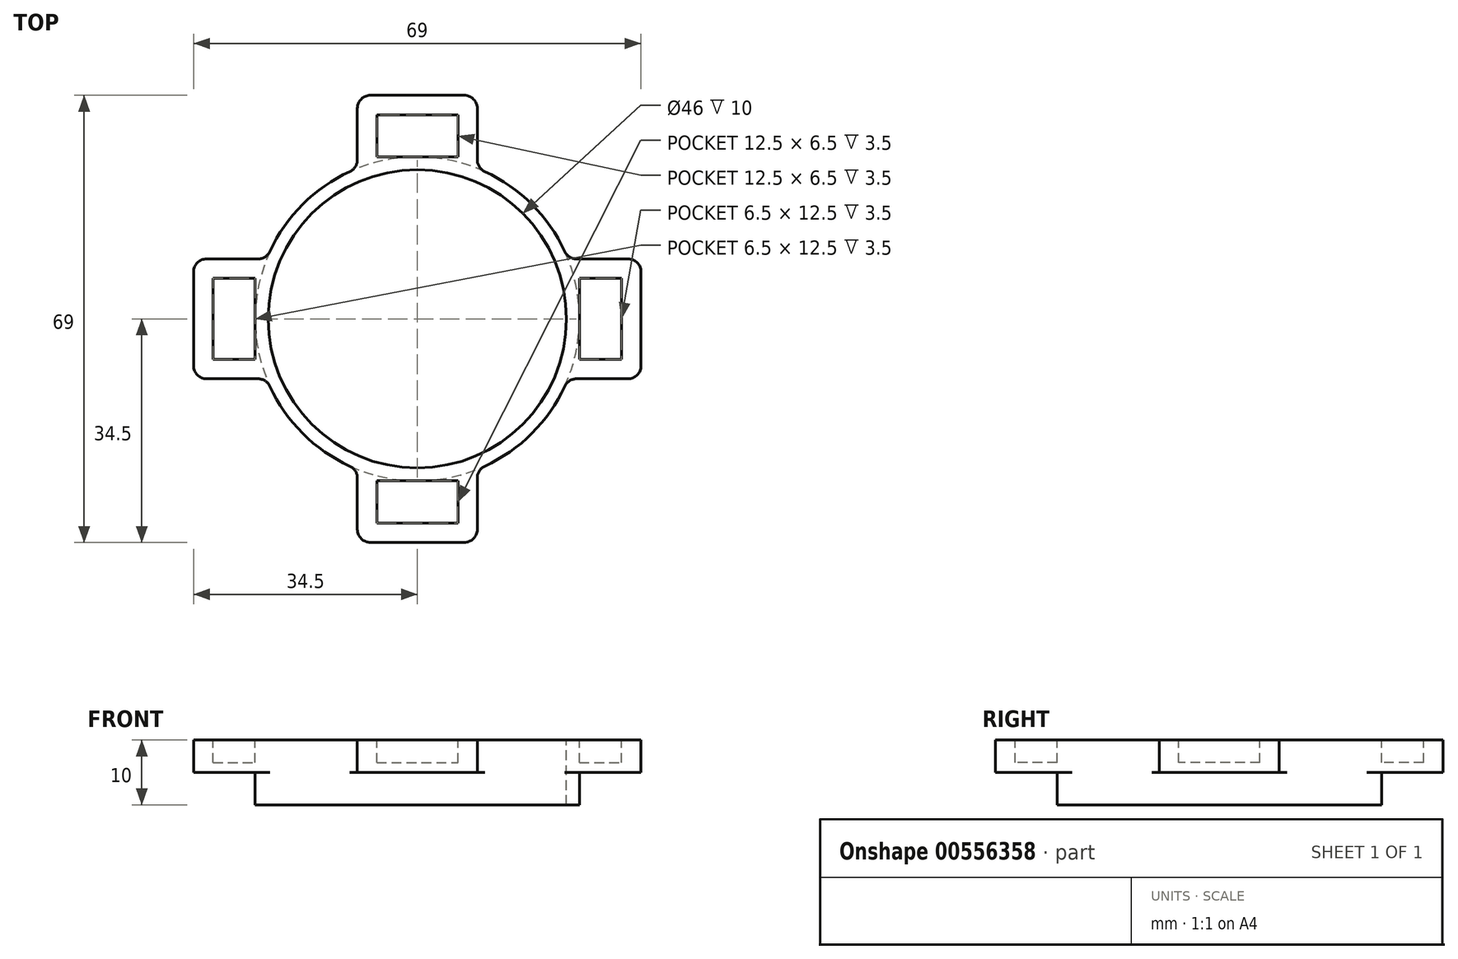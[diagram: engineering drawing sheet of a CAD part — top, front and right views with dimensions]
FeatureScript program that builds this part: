
annotation { "Feature Type Name" : "Feature", "Feature Type Description" : "" }
export const myFeature = defineFeature(function(context is Context, id is Id, definition is map)
    precondition{}
    {
        {
            var Q0;
            Q0=qCreatedBy(makeId("Top.planeOp"),FACE);
            var sketch = newSketch(context, id + "F0", { "sketchPlane" : qUnion([Q0])});
            skCircle(sketch, "E0", {"center": v(0, 0) * mm, "radius": 31.75 * mm, "construction": true});
            skCircle(sketch, "E1", {"center": v(0, 0) * mm, "radius": 23 * mm});
            skLineSegment(sketch, "E2.bottom", {"start": v(25, 6.25) * mm, "end": v(31.5, 6.25) * mm});
            skLineSegment(sketch, "E2.top", {"start": v(25, -6.25) * mm, "end": v(31.5, -6.25) * mm});
            skLineSegment(sketch, "E2.left", {"start": v(25, 6.25) * mm, "end": v(25, -6.25) * mm});
            skLineSegment(sketch, "E2.right", {"start": v(31.5, 6.25) * mm, "end": v(31.5, -6.25) * mm});
            skPoint(sketch, "E3", {"position": v(25, 0) * mm});
            skCircle(sketch, "E4", {"center": v(0, 0) * mm, "radius": 25 * mm});
            skLineSegment(sketch, "E5.bottom", {"start": v(-31.5, 6.25) * mm, "end": v(-25, 6.25) * mm});
            skLineSegment(sketch, "E5.top", {"start": v(-31.5, -6.25) * mm, "end": v(-25, -6.25) * mm});
            skLineSegment(sketch, "E5.left", {"start": v(-31.5, 6.25) * mm, "end": v(-31.5, -6.25) * mm});
            skLineSegment(sketch, "E5.right", {"start": v(-25, 6.25) * mm, "end": v(-25, -6.25) * mm});
            skPoint(sketch, "E6", {"position": v(-25, 0) * mm});
            skLineSegment(sketch, "E7.bottom", {"start": v(-34.5, 9.25) * mm, "end": v(34.5, 9.25) * mm});
            skLineSegment(sketch, "E7.top", {"start": v(-34.5, -9.25) * mm, "end": v(34.5, -9.25) * mm});
            skLineSegment(sketch, "E7.left", {"start": v(-34.5, 9.25) * mm, "end": v(-34.5, -9.25) * mm});
            skLineSegment(sketch, "E7.right", {"start": v(34.5, 9.25) * mm, "end": v(34.5, -9.25) * mm});
            skCircle(sketch, "E8", {"center": v(0, 0) * mm, "radius": 19.05 * mm});
            skLineSegment(sketch, "E9.bottom", {"start": v(-9.25, 34.5) * mm, "end": v(9.25, 34.5) * mm});
            skLineSegment(sketch, "E9.top", {"start": v(-9.25, -34.5) * mm, "end": v(9.25, -34.5) * mm});
            skLineSegment(sketch, "E9.left", {"start": v(-9.25, 34.5) * mm, "end": v(-9.25, -34.5) * mm});
            skLineSegment(sketch, "E9.right", {"start": v(9.25, 34.5) * mm, "end": v(9.25, -34.5) * mm});
            skLineSegment(sketch, "E10.bottom", {"start": v(-6.25, 31.5) * mm, "end": v(6.25, 31.5) * mm});
            skLineSegment(sketch, "E10.top", {"start": v(-6.25, 25) * mm, "end": v(6.25, 25) * mm});
            skLineSegment(sketch, "E10.left", {"start": v(-6.25, 31.5) * mm, "end": v(-6.25, 25) * mm});
            skLineSegment(sketch, "E10.right", {"start": v(6.25, 31.5) * mm, "end": v(6.25, 25) * mm});
            skLineSegment(sketch, "E11.bottom", {"start": v(-6.25, -25) * mm, "end": v(6.25, -25) * mm});
            skLineSegment(sketch, "E11.top", {"start": v(-6.25, -31.5) * mm, "end": v(6.25, -31.5) * mm});
            skLineSegment(sketch, "E11.left", {"start": v(-6.25, -25) * mm, "end": v(-6.25, -31.5) * mm});
            skLineSegment(sketch, "E11.right", {"start": v(6.25, -25) * mm, "end": v(6.25, -31.5) * mm});
            skPoint(sketch, "E12", {"position": v(0, -25) * mm});
            skSolve(sketch);
        }
        {
            var Q0;
            {var subQ0=sQuery(id+"F0.wireOp",EDGE,"E5.bottom");Q0=makeQuery(id+"F0.imprint","IMPRINT",FACE,{"disambiguationData":[TD([[makeQuery(id+"F0.imprint","IMPRINT",EDGE,{"derivedFrom":subQ0}),1.0]])]});}
            var Q1;
            {var subQ4=sQuery(id+"F0.wireOp",EDGE,"E2.bottom");Q1=makeQuery(id+"F0.imprint","IMPRINT",FACE,{"disambiguationData":[TD([[makeQuery(id+"F0.imprint","IMPRINT",EDGE,{"derivedFrom":subQ4}),1.0]])]});}
            var Q2;
            {var subQ0=sQuery(id+"F0.wireOp",EDGE,"E7.top");var subQ1=sQuery(id+"F0.wireOp",EDGE,"9AU1a6xc-WkkM-5iDV-fBZs-smRrCXbzpLaA");var subQ2=makeQuery(id+"F0.imprint","INTERSECT",VERTEX,{"disambiguationData":[OD(0.0)],"derivedFrom":[subQ1,subQ0]});Q2=makeQuery(id+"F0.imprint","IMPRINT",FACE,{"disambiguationData":[TD([[makeQuery(id+"F0.imprint","IMPRINT",EDGE,{"disambiguationData":[TD([[subQ2,-1.0]])],"derivedFrom":subQ1}),-1.0]])]});}
            var Q3;
            {var subQ0=sQuery(id+"F0.wireOp",EDGE,"E7.bottom");var subQ3=sQuery(id+"F0.wireOp",EDGE,"9AU1a6xc-WkkM-5iDV-fBZs-smRrCXbzpLaA");var subQ4=makeQuery(id+"F0.imprint","INTERSECT",VERTEX,{"disambiguationData":[OD(1.0)],"derivedFrom":[subQ3,subQ0]});Q3=makeQuery(id+"F0.imprint","IMPRINT",FACE,{"disambiguationData":[TD([[makeQuery(id+"F0.imprint","IMPRINT",EDGE,{"disambiguationData":[TD([[subQ4,1.0]])],"derivedFrom":subQ3}),-1.0]])]});}
            var Q4;
            {var subQ0=sQuery(id+"F0.wireOp",EDGE,"E7.bottom");var subQ1=sQuery(id+"F0.wireOp",EDGE,"9AU1a6xc-WkkM-5iDV-fBZs-smRrCXbzpLaA");var subQ2=makeQuery(id+"F0.imprint","INTERSECT",VERTEX,{"disambiguationData":[OD(0.0)],"derivedFrom":[subQ1,subQ0]});Q4=makeQuery(id+"F0.imprint","IMPRINT",FACE,{"disambiguationData":[TD([[makeQuery(id+"F0.imprint","IMPRINT",EDGE,{"disambiguationData":[TD([[subQ2,1.0]])],"derivedFrom":subQ1}),-1.0]])]});}
            var Q5;
            {var subQ0=sQuery(id+"F0.wireOp",EDGE,"E7.bottom");var subQ3=sQuery(id+"F0.wireOp",EDGE,"9AU1a6xc-WkkM-5iDV-fBZs-smRrCXbzpLaA");var subQ4=makeQuery(id+"F0.imprint","INTERSECT",VERTEX,{"disambiguationData":[OD(0.0)],"derivedFrom":[subQ3,subQ0]});Q5=makeQuery(id+"F0.imprint","IMPRINT",FACE,{"disambiguationData":[TD([[makeQuery(id+"F0.imprint","IMPRINT",EDGE,{"disambiguationData":[TD([[subQ4,-1.0]])],"derivedFrom":subQ3}),-1.0]])]});}
            var Q6;
            {var subQ0=sQuery(id+"F0.wireOp",EDGE,"E7.bottom");var subQ1=sQuery(id+"F0.wireOp",EDGE,"9AU1a6xc-WkkM-5iDV-fBZs-smRrCXbzpLaA");var subQ2=makeQuery(id+"F0.imprint","INTERSECT",VERTEX,{"disambiguationData":[OD(0.0)],"derivedFrom":[subQ1,subQ0]});Q6=makeQuery(id+"F0.imprint","IMPRINT",FACE,{"disambiguationData":[TD([[makeQuery(id+"F0.imprint","IMPRINT",EDGE,{"disambiguationData":[TD([[subQ2,-1.0]])],"derivedFrom":subQ1}),1.0]])]});}
            var Q7;
            {var subQ0=sQuery(id+"F0.wireOp",EDGE,"E7.bottom");var subQ1=sQuery(id+"F0.wireOp",EDGE,"9AU1a6xc-WkkM-5iDV-fBZs-smRrCXbzpLaA");var subQ2=makeQuery(id+"F0.imprint","INTERSECT",VERTEX,{"disambiguationData":[OD(1.0)],"derivedFrom":[subQ1,subQ0]});Q7=makeQuery(id+"F0.imprint","IMPRINT",FACE,{"disambiguationData":[TD([[makeQuery(id+"F0.imprint","IMPRINT",EDGE,{"disambiguationData":[TD([[subQ2,1.0]])],"derivedFrom":subQ1}),1.0]])]});}
            var Q8;
            {var subQ0=sQuery(id+"F0.wireOp",EDGE,"E7.bottom");var subQ1=sQuery(id+"F0.wireOp",EDGE,"9AU1a6xc-WkkM-5iDV-fBZs-smRrCXbzpLaA");var subQ2=makeQuery(id+"F0.imprint","INTERSECT",VERTEX,{"disambiguationData":[OD(0.0)],"derivedFrom":[subQ1,subQ0]});Q8=makeQuery(id+"F0.imprint","IMPRINT",FACE,{"disambiguationData":[TD([[makeQuery(id+"F0.imprint","IMPRINT",EDGE,{"disambiguationData":[TD([[subQ2,1.0]])],"derivedFrom":subQ1}),1.0]])]});}
            var Q9;
            {var subQ0=sQuery(id+"F0.wireOp",EDGE,"E7.top");var subQ1=sQuery(id+"F0.wireOp",EDGE,"9AU1a6xc-WkkM-5iDV-fBZs-smRrCXbzpLaA");var subQ2=makeQuery(id+"F0.imprint","INTERSECT",VERTEX,{"disambiguationData":[OD(0.0)],"derivedFrom":[subQ1,subQ0]});Q9=makeQuery(id+"F0.imprint","IMPRINT",FACE,{"disambiguationData":[TD([[makeQuery(id+"F0.imprint","IMPRINT",EDGE,{"disambiguationData":[TD([[subQ2,-1.0]])],"derivedFrom":subQ1}),1.0]])]});}
            var Q10;
            {var subQ1=sQuery(id+"F0.wireOp",EDGE,"E5.bottom");Q10=makeQuery(id+"F0.imprint","IMPRINT",FACE,{"disambiguationData":[TD([[makeQuery(id+"F0.imprint","IMPRINT",EDGE,{"derivedFrom":subQ1}),-1.0]])]});}
            var Q11;
            {var subQ3=sQuery(id+"F0.wireOp",EDGE,"E2.bottom");Q11=makeQuery(id+"F0.imprint","IMPRINT",FACE,{"disambiguationData":[TD([[makeQuery(id+"F0.imprint","IMPRINT",EDGE,{"derivedFrom":subQ3}),-1.0]])]});}
            var Q12;
            {var subQ0=sQuery(id+"F0.wireOp",EDGE,"E7.bottom");var subQ1=sQuery(id+"F0.wireOp",EDGE,"E1");var subQ2=makeQuery(id+"F0.imprint","INTERSECT",VERTEX,{"disambiguationData":[OD(0.0)],"derivedFrom":[subQ1,subQ0]});Q12=makeQuery(id+"F0.imprint","IMPRINT",FACE,{"disambiguationData":[TD([[makeQuery(id+"F0.imprint","IMPRINT",EDGE,{"disambiguationData":[TD([[subQ2,1.0]])],"derivedFrom":subQ1}),-1.0]])]});}
            var Q13;
            {var subQ4=sQuery(id+"F0.wireOp",EDGE,"E7.bottom");var subQ5=sQuery(id+"F0.wireOp",EDGE,"E1");var subQ6=makeQuery(id+"F0.imprint","INTERSECT",VERTEX,{"disambiguationData":[OD(0.0)],"derivedFrom":[subQ5,subQ4]});Q13=makeQuery(id+"F0.imprint","IMPRINT",FACE,{"disambiguationData":[TD([[makeQuery(id+"F0.imprint","IMPRINT",EDGE,{"disambiguationData":[TD([[subQ6,-1.0]])],"derivedFrom":subQ5}),-1.0]])]});}
            var Q14;
            {var subQ4=sQuery(id+"F0.wireOp",EDGE,"E7.bottom");var subQ5=sQuery(id+"F0.wireOp",EDGE,"E1");var subQ6=makeQuery(id+"F0.imprint","INTERSECT",VERTEX,{"disambiguationData":[OD(1.0)],"derivedFrom":[subQ5,subQ4]});Q14=makeQuery(id+"F0.imprint","IMPRINT",FACE,{"disambiguationData":[TD([[makeQuery(id+"F0.imprint","IMPRINT",EDGE,{"disambiguationData":[TD([[subQ6,1.0]])],"derivedFrom":subQ5}),-1.0]])]});}
            var Q15;
            {var subQ0=sQuery(id+"F0.wireOp",EDGE,"E7.top");var subQ1=sQuery(id+"F0.wireOp",EDGE,"E1");var subQ2=makeQuery(id+"F0.imprint","INTERSECT",VERTEX,{"disambiguationData":[OD(0.0)],"derivedFrom":[subQ1,subQ0]});Q15=makeQuery(id+"F0.imprint","IMPRINT",FACE,{"disambiguationData":[TD([[makeQuery(id+"F0.imprint","IMPRINT",EDGE,{"disambiguationData":[TD([[subQ2,-1.0]])],"derivedFrom":subQ1}),-1.0]])]});}
            var Q16;
            {var subQ0=sQuery(id+"F0.wireOp",EDGE,"E7.bottom");var subQ3=sQuery(id+"F0.wireOp",EDGE,"E1");var subQ4=makeQuery(id+"F0.imprint","INTERSECT",VERTEX,{"disambiguationData":[OD(1.0)],"derivedFrom":[subQ3,subQ0]});Q16=makeQuery(id+"F0.imprint","IMPRINT",FACE,{"disambiguationData":[TD([[makeQuery(id+"F0.imprint","IMPRINT",EDGE,{"disambiguationData":[TD([[subQ4,-1.0]])],"derivedFrom":subQ3}),-1.0]])]});}
            var Q17;
            {var subQ0=sQuery(id+"F0.wireOp",EDGE,"E9.right");var subQ4=sQuery(id+"F0.wireOp",EDGE,"E1");var subQ5=makeQuery(id+"F0.imprint","INTERSECT",VERTEX,{"disambiguationData":[OD(0.0)],"derivedFrom":[subQ4,subQ0]});Q17=makeQuery(id+"F0.imprint","IMPRINT",FACE,{"disambiguationData":[TD([[makeQuery(id+"F0.imprint","IMPRINT",EDGE,{"disambiguationData":[TD([[subQ5,-1.0]])],"derivedFrom":subQ4}),-1.0]])]});}
            var Q18;
            {var subQ0=sQuery(id+"F0.wireOp",EDGE,"E9.right");var subQ1=sQuery(id+"F0.wireOp",EDGE,"E1");var subQ2=makeQuery(id+"F0.imprint","INTERSECT",VERTEX,{"disambiguationData":[OD(1.0)],"derivedFrom":[subQ1,subQ0]});Q18=makeQuery(id+"F0.imprint","IMPRINT",FACE,{"disambiguationData":[TD([[makeQuery(id+"F0.imprint","IMPRINT",EDGE,{"disambiguationData":[TD([[subQ2,-1.0]])],"derivedFrom":subQ1}),-1.0]])]});}
            var Q19;
            {var subQ0=sQuery(id+"F0.wireOp",EDGE,"E9.left");var subQ3=sQuery(id+"F0.wireOp",EDGE,"E1");var subQ4=makeQuery(id+"F0.imprint","INTERSECT",VERTEX,{"disambiguationData":[OD(1.0)],"derivedFrom":[subQ3,subQ0]});Q19=makeQuery(id+"F0.imprint","IMPRINT",FACE,{"disambiguationData":[TD([[makeQuery(id+"F0.imprint","IMPRINT",EDGE,{"disambiguationData":[TD([[subQ4,-1.0]])],"derivedFrom":subQ3}),-1.0]])]});}
            var Q20;
            {var subQ1=sQuery(id+"F0.wireOp",EDGE,"E9.top");Q20=makeQuery(id+"F0.imprint","IMPRINT",FACE,{"disambiguationData":[TD([[makeQuery(id+"F0.imprint","IMPRINT",EDGE,{"derivedFrom":subQ1}),1.0]])]});}
            var Q21;
            Q21=makeQuery(id+"F0.imprint","IMPRINT",FACE,{"disambiguationData":[TD([[makeQuery(id+"F0.imprint","IMPRINT",EDGE,{"derivedFrom":sQuery(id+"F0.wireOp",EDGE,"E11.top")}),1.0]])]});
            var Q22;
            {var subQ0=sQuery(id+"F0.wireOp",EDGE,"E9.bottom");Q22=makeQuery(id+"F0.imprint","IMPRINT",FACE,{"disambiguationData":[TD([[makeQuery(id+"F0.imprint","IMPRINT",EDGE,{"derivedFrom":subQ0}),-1.0]])]});}
            var Q23;
            Q23=makeQuery(id+"F0.imprint","IMPRINT",FACE,{"disambiguationData":[TD([[makeQuery(id+"F0.imprint","IMPRINT",EDGE,{"derivedFrom":sQuery(id+"F0.wireOp",EDGE,"E10.bottom")}),-1.0]])]});
            extrude(context, id + "F1", {"entities" : qUnion([Q0, Q1, Q2, Q3, Q4, Q5, Q6, Q7, Q8, Q9, Q10, Q11, Q12, Q13, Q14, Q15, Q16, Q17, Q18, Q19, Q20, Q21, Q22, Q23]), "oppositeDirection" : true, "depth" : 5 * mm, "offsetDistance" : 25 * mm});
        }
        {
            var Q0;
            {var subQ1=sQuery(id+"F0.wireOp",EDGE,"E5.bottom");Q0=makeQuery(id+"F0.imprint","IMPRINT",FACE,{"disambiguationData":[TD([[makeQuery(id+"F0.imprint","IMPRINT",EDGE,{"derivedFrom":subQ1}),-1.0]])]});}
            var Q1;
            {var subQ3=sQuery(id+"F0.wireOp",EDGE,"E2.bottom");Q1=makeQuery(id+"F0.imprint","IMPRINT",FACE,{"disambiguationData":[TD([[makeQuery(id+"F0.imprint","IMPRINT",EDGE,{"derivedFrom":subQ3}),-1.0]])]});}
            var Q2;
            Q2=makeQuery(id+"F0.imprint","IMPRINT",FACE,{"disambiguationData":[TD([[makeQuery(id+"F0.imprint","IMPRINT",EDGE,{"derivedFrom":sQuery(id+"F0.wireOp",EDGE,"E10.bottom")}),-1.0]])]});
            var Q3;
            Q3=makeQuery(id+"F0.imprint","IMPRINT",FACE,{"disambiguationData":[TD([[makeQuery(id+"F0.imprint","IMPRINT",EDGE,{"derivedFrom":sQuery(id+"F0.wireOp",EDGE,"E11.top")}),1.0]])]});
            extrude(context, id + "F2", {"entities" : qUnion([Q0, Q1, Q2, Q3]), "operationType" : NewBodyOperationType.REMOVE, "oppositeDirection" : true, "depth" : 3.5 * mm, "offsetDistance" : 25 * mm});
        }
        {
            var Q0;
            Q0=makeQuery(id+"F1.opExtrude","SWEPT_EDGE",EDGE,{"disambiguationData":[OSD([sQuery(id+"F0.wireOp",EDGE,"E7.bottom"),sQuery(id+"F0.wireOp",EDGE,"E7.left")])]});
            var Q1;
            Q1=makeQuery(id+"F1.opExtrude","SWEPT_EDGE",EDGE,{"disambiguationData":[OSD([sQuery(id+"F0.wireOp",EDGE,"E7.top"),sQuery(id+"F0.wireOp",EDGE,"E7.left")])]});
            var Q2;
            Q2=makeQuery(id+"F1.opExtrude","SWEPT_EDGE",EDGE,{"disambiguationData":[OSD([sQuery(id+"F0.wireOp",EDGE,"E7.bottom"),sQuery(id+"F0.wireOp",EDGE,"E7.right")])]});
            var Q3;
            {var subQ0=sQuery(id+"F0.wireOp",EDGE,"E7.top");var subQ1=sQuery(id+"F0.wireOp",EDGE,"E4");Q3=makeQuery(id+"F1.opExtrude","SWEPT_EDGE",EDGE,{"disambiguationData":[OSD([subQ1,subQ0]),TDD([makeQuery(id+"F0.imprint","INTERSECT",VERTEX,{"disambiguationData":[OD(1.0)],"derivedFrom":[subQ1,subQ0]})])]});}
            var Q4;
            Q4=makeQuery(id+"F1.opExtrude","SWEPT_EDGE",EDGE,{"disambiguationData":[OSD([sQuery(id+"F0.wireOp",EDGE,"E7.top"),sQuery(id+"F0.wireOp",EDGE,"E7.right")])]});
            var Q5;
            {var subQ0=sQuery(id+"F0.wireOp",EDGE,"E7.top");var subQ1=sQuery(id+"F0.wireOp",EDGE,"E4");Q5=makeQuery(id+"F1.opExtrude","SWEPT_EDGE",EDGE,{"disambiguationData":[OSD([subQ1,subQ0]),TDD([makeQuery(id+"F0.imprint","INTERSECT",VERTEX,{"disambiguationData":[OD(0.0)],"derivedFrom":[subQ1,subQ0]})])]});}
            var Q6;
            {var subQ0=sQuery(id+"F0.wireOp",EDGE,"E7.bottom");var subQ1=sQuery(id+"F0.wireOp",EDGE,"E4");Q6=makeQuery(id+"F1.opExtrude","SWEPT_EDGE",EDGE,{"disambiguationData":[OSD([subQ1,subQ0]),TDD([makeQuery(id+"F0.imprint","INTERSECT",VERTEX,{"disambiguationData":[OD(0.0)],"derivedFrom":[subQ1,subQ0]})])]});}
            var Q7;
            Q7=makeQuery(id+"F1.opExtrude","SWEPT_EDGE",EDGE,{"disambiguationData":[OSD([sQuery(id+"F0.wireOp",EDGE,"E9.bottom"),sQuery(id+"F0.wireOp",EDGE,"E9.right")])]});
            var Q8;
            {var subQ0=sQuery(id+"F0.wireOp",EDGE,"E9.right");var subQ1=sQuery(id+"F0.wireOp",EDGE,"E4");Q8=makeQuery(id+"F1.opExtrude","SWEPT_EDGE",EDGE,{"disambiguationData":[OSD([subQ1,subQ0]),TDD([makeQuery(id+"F0.imprint","INTERSECT",VERTEX,{"disambiguationData":[OD(0.0)],"derivedFrom":[subQ1,subQ0]})])]});}
            var Q9;
            Q9=makeQuery(id+"F1.opExtrude","SWEPT_EDGE",EDGE,{"disambiguationData":[OSD([sQuery(id+"F0.wireOp",EDGE,"E9.top"),sQuery(id+"F0.wireOp",EDGE,"E9.right")])]});
            var Q10;
            Q10=makeQuery(id+"F1.opExtrude","SWEPT_EDGE",EDGE,{"disambiguationData":[OSD([sQuery(id+"F0.wireOp",EDGE,"E9.top"),sQuery(id+"F0.wireOp",EDGE,"E9.left")])]});
            var Q11;
            {var subQ0=sQuery(id+"F0.wireOp",EDGE,"E9.left");var subQ1=sQuery(id+"F0.wireOp",EDGE,"E4");Q11=makeQuery(id+"F1.opExtrude","SWEPT_EDGE",EDGE,{"disambiguationData":[OSD([subQ1,subQ0]),TDD([makeQuery(id+"F0.imprint","INTERSECT",VERTEX,{"disambiguationData":[OD(1.0)],"derivedFrom":[subQ1,subQ0]})])]});}
            var Q12;
            {var subQ0=sQuery(id+"F0.wireOp",EDGE,"E9.right");var subQ1=sQuery(id+"F0.wireOp",EDGE,"E4");Q12=makeQuery(id+"F1.opExtrude","SWEPT_EDGE",EDGE,{"disambiguationData":[OSD([subQ1,subQ0]),TDD([makeQuery(id+"F0.imprint","INTERSECT",VERTEX,{"disambiguationData":[OD(1.0)],"derivedFrom":[subQ1,subQ0]})])]});}
            var Q13;
            Q13=makeQuery(id+"F1.opExtrude","SWEPT_EDGE",EDGE,{"disambiguationData":[OSD([sQuery(id+"F0.wireOp",EDGE,"E9.bottom"),sQuery(id+"F0.wireOp",EDGE,"E9.left")])]});
            var Q14;
            {var subQ0=sQuery(id+"F0.wireOp",EDGE,"E9.left");var subQ1=sQuery(id+"F0.wireOp",EDGE,"E4");Q14=makeQuery(id+"F1.opExtrude","SWEPT_EDGE",EDGE,{"disambiguationData":[OSD([subQ1,subQ0]),TDD([makeQuery(id+"F0.imprint","INTERSECT",VERTEX,{"disambiguationData":[OD(0.0)],"derivedFrom":[subQ1,subQ0]})])]});}
            var Q15;
            {var subQ0=sQuery(id+"F0.wireOp",EDGE,"E7.bottom");var subQ1=sQuery(id+"F0.wireOp",EDGE,"E4");Q15=makeQuery(id+"F1.opExtrude","SWEPT_EDGE",EDGE,{"disambiguationData":[OSD([subQ1,subQ0]),TDD([makeQuery(id+"F0.imprint","INTERSECT",VERTEX,{"disambiguationData":[OD(1.0)],"derivedFrom":[subQ1,subQ0]})])]});}
            fillet(context, id + "F3", {"entities" : qUnion([Q0, Q1, Q2, Q3, Q4, Q5, Q6, Q7, Q8, Q9, Q10, Q11, Q12, Q13, Q14, Q15]), "radius" : 2 * mm, "tangentPropagation" : true, "allowEdgeOverflow" : false});
        }
        {
            var Q0;
            Q0=makeQuery(id+"F1.opExtrude","CAP_FACE",FACE,{"disambiguationData":[OSD([sQuery(id+"F0.wireOp",EDGE,"E1"),sQuery(id+"F0.wireOp",EDGE,"E4"),sQuery(id+"F0.wireOp",EDGE,"E7.bottom"),sQuery(id+"F0.wireOp",EDGE,"E7.top"),sQuery(id+"F0.wireOp",EDGE,"E7.left"),sQuery(id+"F0.wireOp",EDGE,"E7.right")])],"isStart":false});
            var sketch = newSketch(context, id + "F4", { "sketchPlane" : qUnion([Q0])});
            skCircle(sketch, "E13", {"center": v(0, 0) * mm, "radius": 25 * mm});
            skCircle(sketch, "E14", {"center": v(0, 0) * mm, "radius": 23 * mm});
            skSolve(sketch);
        }
        {
            var Q0;
            Q0=makeQuery(id+"F4.imprint","IMPRINT",FACE,{"disambiguationData":[TD([[makeQuery(id+"F4.imprint","IMPRINT",EDGE,{"derivedFrom":sQuery(id+"F4.wireOp",EDGE,"E14")}),1.0]])]});
            extrude(context, id + "F5", {"entities" : qUnion([Q0]), "operationType" : NewBodyOperationType.ADD, "depth" : 5 * mm, "offsetDistance" : 25 * mm});
        }
    });
